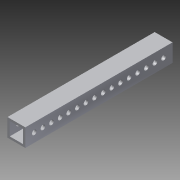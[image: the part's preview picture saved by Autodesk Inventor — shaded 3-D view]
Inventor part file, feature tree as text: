
AUTODESK INVENTOR PART (.ipt)
format: ipt  version: 2013 (Build 170138000, 138)  size: 133,120 bytes
history: native  units: in
note: dims shown in document units (in); Inventor stores cm internally (conversion verified against a paired STEP export)
features: extrude x2, sketch x1
ambient origin geometry x8: Origin, YZ Plane, XZ Plane, XY Plane, X Axis, Y Axis, Z Axis, Center Point
bodies: Solid1 (feature_tree)
feature tree (3):
  extrude  "Extrusion1"  Depth=1.0in
  extrude  "Extrusion2"  Depth=0.125in
  sketch  "Sketch1"  dims[d0=1.0in d1=1.0in d2=0.125in d3=8.25in d4=0.0in d5=0.5in d7=0.26in d8=16.5in d9=0.0in d13=8.25in d14=6.2992in d16=0.4833in d17=0.3937in d19=1.0in]
